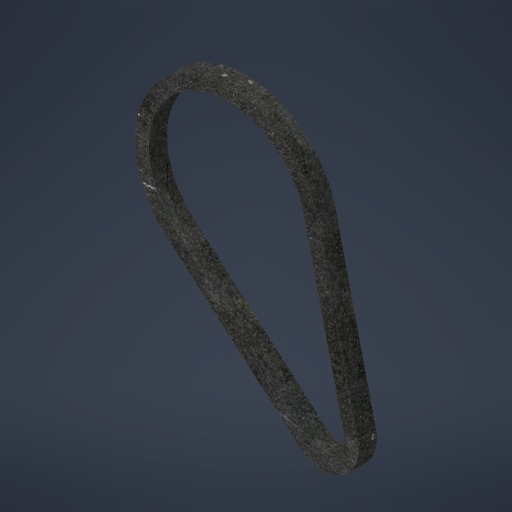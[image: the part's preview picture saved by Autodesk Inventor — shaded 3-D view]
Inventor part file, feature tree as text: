
AUTODESK INVENTOR PART (.ipt)
format: ipt  version: 2023.4 (Build 274418000, 418)  size: 260,096 bytes
history: native  units: in
note: dims shown in document units (in); Inventor stores cm internally (conversion verified against a paired STEP export)
features: extrude x1, sketch x1
ambient origin geometry x8: Origin, YZ Plane, XZ Plane, XY Plane, X Axis, Y Axis, Z Axis, Center Point
bodies: Solid1 (feature_tree)
feature tree (2):
  extrude  "Extrusion1"  Depth=0.466in
  sketch  "Sketch1"  dims[d0=1.432in d1=4.297in d2=4.6532in d3=0.347in d4=2.4094in d5=0.1735in d6=0.466in d7=0.0in]
